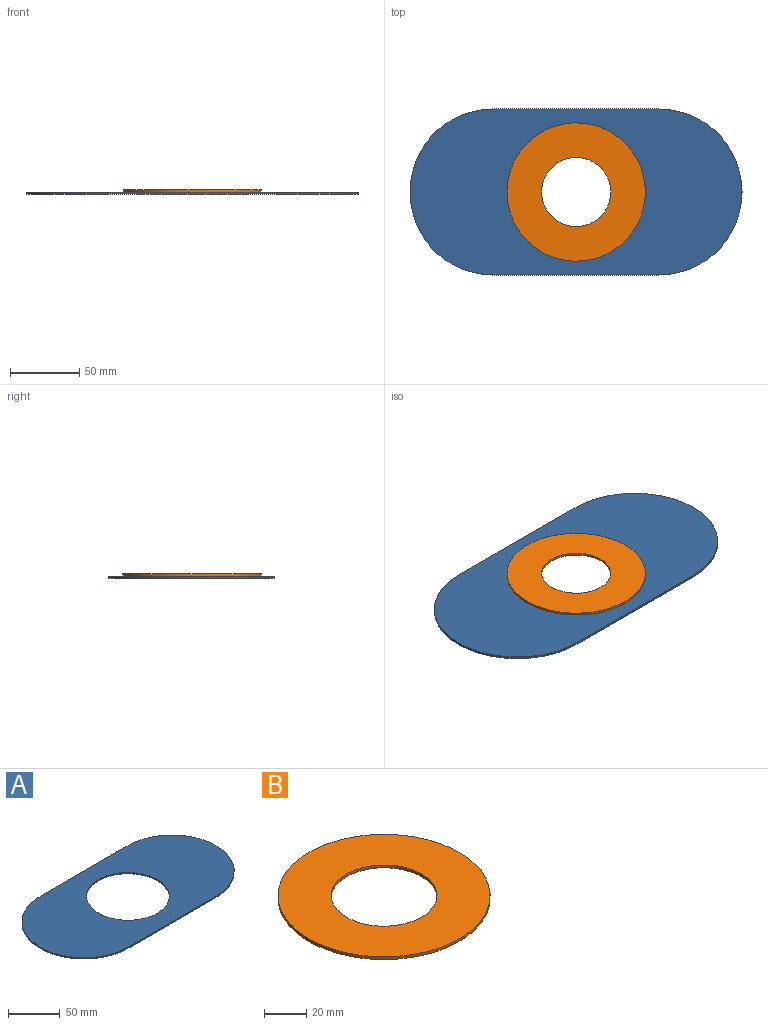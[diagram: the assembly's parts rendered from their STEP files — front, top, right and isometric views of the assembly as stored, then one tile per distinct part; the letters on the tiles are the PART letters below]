
ASSEMBLY  parts=2 mates=1
PART A: 7 faces, bbox 240x120x1.6 mm
  f0: plane 120x1.59mm, normal (0,1,0), area 190.5mm2, adj f1,f3,f4,f5
  f1: cylinder r=60mm len=120mm, axis (0,0,-1), area 299.2mm2, adj f0,f2,f4,f5
  f2: plane 120x1.59mm, normal (0,-1,0), area 190.5mm2, adj f1,f3,f4,f5
  f3: cylinder r=60mm len=120mm, axis (0,0,-1), area 299.2mm2, adj f0,f2,f4,f5
  f4: plane 240x120mm, normal (0,0,1), area 20683.2mm2, adj f0,f1,f2,f3,f6
  f5: plane 240x120mm, normal (0,0,-1), area 20683.2mm2, adj f0,f1,f2,f3,f6
  f6: cylinder r=40mm len=80mm, axis (0,0,1), area 399mm2, adj f4,f5
PART B: 4 faces, bbox 100x100x1.6 mm
  f0: cylinder r=50mm len=100mm, axis (0,0,-1), area 498.7mm2, adj f1,f2
  f1: plane 100x100mm, normal (0,0,1), area 5890.5mm2, adj f0,f3
  f2: plane 100x100mm, normal (0,0,-1), area 5890.5mm2, adj f0,f3
  f3: cylinder r=25mm len=50mm, axis (0,0,-1), area 249.4mm2, adj f1,f2
PLACE A t=(0.03,-0.33,-0.12)mm
PLACE B t=(-22.21,-0.36,1.47)mm
MATE planar B.f0 <-> A.f6  axis (0,0,-1) through (-22.21,-0.36,1.47)mm
